# Revit family: Specialty_Access_Door-Acudor-Surface_Mounted-SF-2000_Series
name_source: partatom
category: Specialty Equipment
revit_build: Autodesk Revit 2014 (Build: 20130308_1515(x64)
units: mm (PartAtom-declared; Revit-internal decimal feet)

## types (4) — shared parameters
Allen Head Cam Latch = No
Array Visibility = Yes
Assembly Code = C1020700
Cylinder Lock = Yes
Default Elevation = 48"
Description = Fully Gasketed Access Door
Finish = Steel-Acudor-16 Gauge-Alkyd White Enamel
Installation Type = Wall Mounted
Length = 1/8"
Manufacturer = Acudor
Material = Steel-Acudor-16 Gauge-Alkyd White Enamel
Mortise Cylinder Lock (Prepare for/or Installed) = No
Product Documentation Link = https://acudor.com
Product Page URL = https://acudor.com
Screwdriver Operated Cam Latch = No
Single Latch Visibility = No
Spanner Head Cam Latch = No
Torx Cam Latch = No
URL = http://acudor.com

## per-type parameters (varying)
| type | First Offset | Height | Latch Count | Latch Spacing | Width |
| SF-2000 8x8 | 2" | 8" | 2 | 4" | 8" |
| SF-2000 12x12 | 3" | 12" | 2 | 6" | 12" |
| SF-2000 16x16 | 4" | 16" | 2 | 8" | 16" |
| SF-2000 24x24 | 3" | 24" | 4 | 6" | 24" |

note: column(s) folded — value = type name in every type: Model

## geometry (parser evidence)
native form markers: Sweep x4
no freeform markers — native parametric forms only
